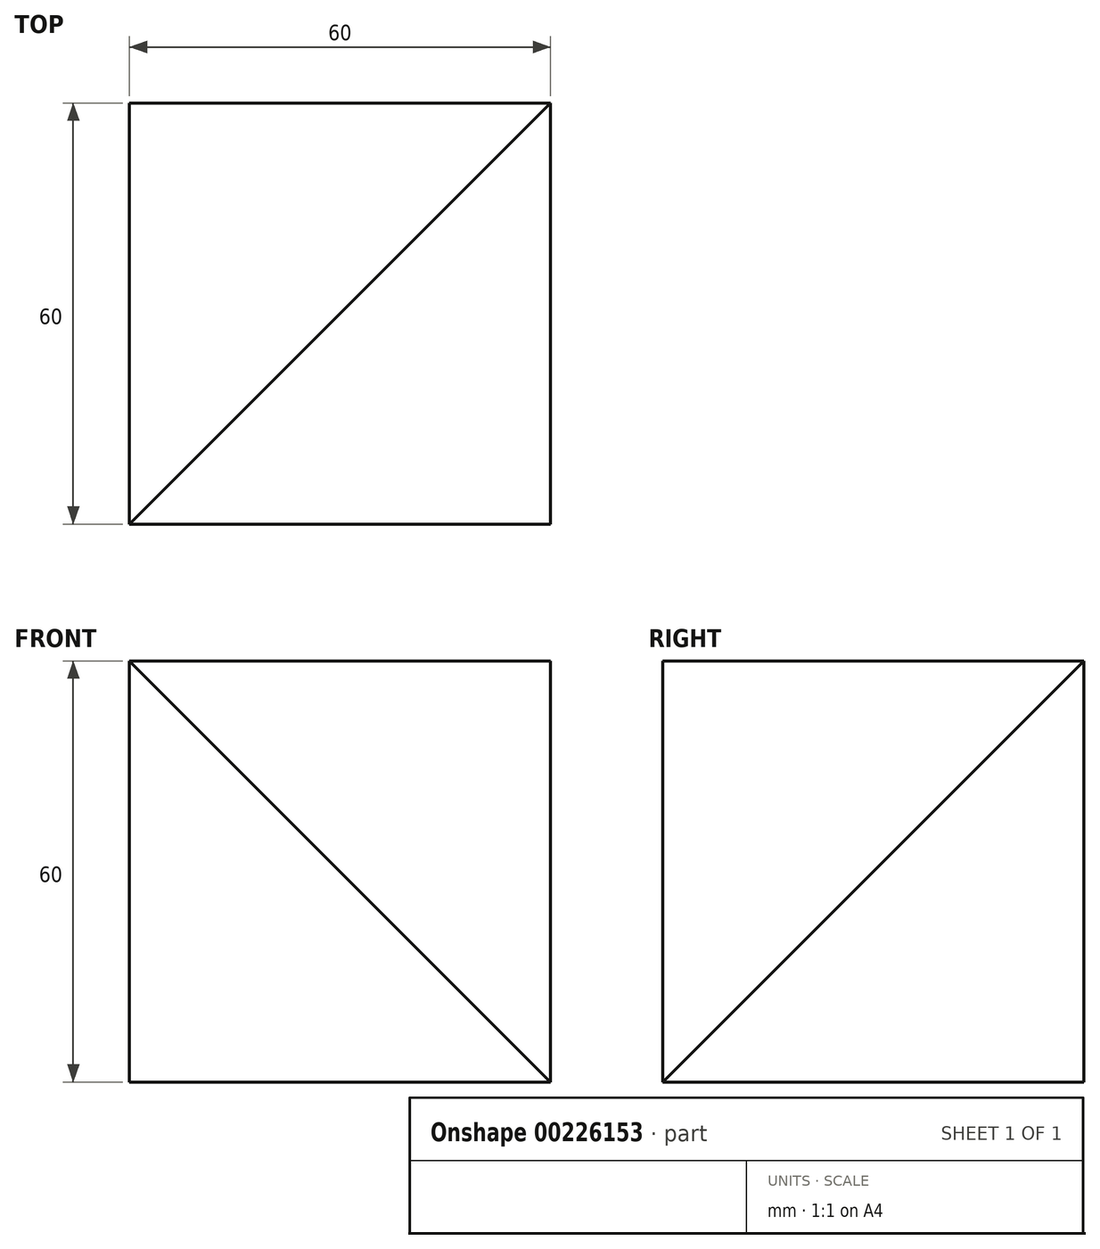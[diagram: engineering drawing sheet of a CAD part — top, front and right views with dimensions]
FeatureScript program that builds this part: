
annotation { "Feature Type Name" : "Feature", "Feature Type Description" : "" }
export const myFeature = defineFeature(function(context is Context, id is Id, definition is map)
    precondition{}
    {
        {
            var Q0;
            Q0=qCreatedBy(makeId("Top.planeOp"),FACE);
            var sketch = newSketch(context, id + "F0", { "sketchPlane" : qUnion([Q0])});
            skLineSegment(sketch, "E0.bottom", {"start": v(0, 0) * mm, "end": v(60, 0) * mm});
            skLineSegment(sketch, "E0.top", {"start": v(0, 60) * mm, "end": v(60, 60) * mm});
            skLineSegment(sketch, "E0.left", {"start": v(0, 0) * mm, "end": v(0, 60) * mm});
            skLineSegment(sketch, "E0.right", {"start": v(60, 0) * mm, "end": v(60, 60) * mm});
            skSolve(sketch);
        }
        {
            var Q0;
            Q0 = qSketchRegion(id + "F0", true);
            extrude(context, id + "F1", {"entities" : qUnion([Q0]), "depth" : 60 * mm});
        }
        {
            var Q0;
            Q0=makeQuery(id+"F1.opExtrude","CAP_VERTEX",VERTEX,{"disambiguationData":[OSD([sQuery(id+"F0.wireOp",EDGE,"E0.bottom"),sQuery(id+"F0.wireOp",EDGE,"E0.left")])],"isStart":false});
            var Q1;
            Q1=makeQuery(id+"F1.opExtrude","CAP_VERTEX",VERTEX,{"disambiguationData":[OSD([sQuery(id+"F0.wireOp",EDGE,"E0.top"),sQuery(id+"F0.wireOp",EDGE,"E0.right")])],"isStart":false});
            var Q2;
            Q2=makeQuery(id+"F1.opExtrude","CAP_VERTEX",VERTEX,{"disambiguationData":[OSD([sQuery(id+"F0.wireOp",EDGE,"E0.bottom"),sQuery(id+"F0.wireOp",EDGE,"E0.right")])],"isStart":true});
            cPlane(context, id + "F2", {"entities" : qUnion([Q0, Q1, Q2]), "cplaneType" : CPlaneType.THREE_POINT, "offset" : 25 * mm, "width" : 150 * mm, "height" : 150 * mm});
        }
        {
            var Q0;
            Q0=qCreatedBy(id+"F2.planeOp",FACE);
            var sketch = newSketch(context, id + "F3", { "sketchPlane" : qUnion([Q0])});
            skPoint(sketch, "E1.0", {"position": v(48.99, 84.85) * mm});
            skPoint(sketch, "E2.0", {"position": v(48.99, 0) * mm});
            skPoint(sketch, "E3.0", {"position": v(-24.5, 42.43) * mm});
            skLineSegment(sketch, "E4", {"start": v(-24.5, 42.43) * mm, "end": v(48.99, 84.85) * mm});
            skLineSegment(sketch, "E5", {"start": v(48.99, 84.85) * mm, "end": v(48.99, 0) * mm});
            skLineSegment(sketch, "E6", {"start": v(48.99, 0) * mm, "end": v(-24.5, 42.43) * mm});
            skSolve(sketch);
        }
        {
            var Q0;
            Q0 = qSketchRegion(id + "F3", true);
            extrude(context, id + "F4", {"entities" : qUnion([Q0]), "operationType" : NewBodyOperationType.REMOVE, "endBound" : BoundingType.THROUGH_ALL, "depth" : 25 * mm});
        }
    });
